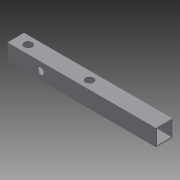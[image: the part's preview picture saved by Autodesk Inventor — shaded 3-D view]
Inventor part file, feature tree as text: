
AUTODESK INVENTOR PART (.ipt)
format: ipt  version: 2014 (Build 180170000, 170)  size: 114,688 bytes
history: native  units: in
note: dims shown in document units (in); Inventor stores cm internally (conversion verified against a paired STEP export)
features: sketch x4, extrude x3, hole x1
ambient origin geometry x8: Origin, YZ Plane, XZ Plane, XY Plane, X Axis, Y Axis, Z Axis, Center Point
bodies: Solid1 (feature_tree)
feature tree (8):
  extrude  "Extrusion1"  Depth=1.0in
  extrude  "Extrusion2"  Depth=8.95in TaperAngle=0.0deg
  extrude  "Extrusion3"  Depth=0.5in
  hole  "Hole1"  [1 undecoded]
  sketch  "Sketch1"  dims[d0=1.0in d1=1.0in]
  sketch  "Sketch2"  dims[d2=0.0625in d3=8.95in d4=0.0in]
  sketch  "Sketch3"  dims[d5=0.5in d6=0.5in]
  sketch  "Sketch4"  dims[d7=0.75in d8=1.0in d9=0.0in d10=0.375in d11=2.0in d12=0.5in d13=1.0in d14=0.0in d15=0.5in d16=4.25in d17=0.5in d18=0.75in d19=0.375in d20=0.25in d21=0.5635in d22=1.0in d23=0.8108in]
note: 1 required parameter value undecoded (feature->parameter linkage not recoverable at this tier; creation-order binding heuristic only, values carry confidence <= 0.55)
